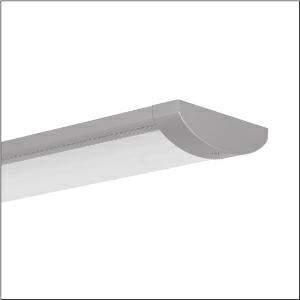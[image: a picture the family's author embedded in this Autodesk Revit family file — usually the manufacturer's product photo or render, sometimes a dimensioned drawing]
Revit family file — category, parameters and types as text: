
# Revit family: tv_20_5xa861d4n0x
name_source: partatom
category: Lighting Fixtures
units: mm (PartAtom-declared; Revit-internal decimal feet)

## family parameters
Cut with Voids When Loaded = No
Host = Face
Light Source = No
Part Type = Normal
Room Calculation Point = No
Round Connector Dimension = Use Diameter
Shared = No

## types (1)
- TV 20 (1 x LED 4000K / CRI = 80 (unbekannt), 5120 lm, 4000K)
    Apparent Load = 50 VA
    CIE Flux Codes = 48 78 95 99 100
    Color Rendering = 80
    Color Temperature = 4000K
    Default Elevation = 1800 mm
    Description = TV 20, vandal-proof luminaire, primary light control with specular reflector, of aluminium, matt, primary optical cover: enclosure, of PC, frosted, light emission: direct distribution, primary light characteristic: symmetric, installation type: surface-mounted, LED, rated luminous flux: 5.120lm, luminous efficacy: 102lm/W, light colour: 840, colour temperature: 4000K, control gear: ECG DALI, mains connection: 230V, AC, 50Hz, rated input power: 50W, luminaire housing, of aluminium, coated, Siteco® metallic grey (DB 702S), with wall and ceiling fixing element, length: 1.561mm, width: 260mm, height: 70mm, protection rating (complete): IP65, insulation class (complete): insulation class I (protective earthing), certification: CE, protection symbol: F, impact resistance: 2x IK10, standard: EN 60598, packaging unit: 1 piece
    Height = 70 mm
    Lamp = 1 x LED 4000K / CRI >= 80 (unbekannt)
    Lamp Light Flux = 5120 lm
    Lamp count = 1
    Length = 1561 mm
    Luminous efficacy = 102 lm/W
    Manufacturer = Siteco
    ModVariant = No
    Model = 5XA861D4N0X
    Mounting Place = Ceiling
    Mounting Type = Surface mounted
    Number of Poles = 1
    OnlyDefault = Yes
    Power Factor = 1
    Product Name = TV 20
    Product group = vandal-proof luminaire
    ProductGroupID = 307
    Protection Class = Protection class I
    Protection Degree = IP 65
    RLX_Detail_Level = 1
    RLX_Emergency_Light_Flux = 0 lm
    RLX_Emergency_Type = 0
    RLX_Emergency_Type_DB = No
    RlxData = <blob elided: 25281 chars, md5=1df7c23b>
    Socket = socket
    Standby Power = 0 W
    System Light Flux = 5120 lm
    System Power = 50 W
    Type Comments = Product without accessories
    Type Image = l_1004809.jpg
    URL = http://relux.com
    VarID = ---
    Voltage = 0 V
    Weight = 0.00 kg
    Width = 260 mm

## geometry (parser evidence)
native form markers: Blend x4, Sweep x10
no freeform markers — native parametric forms only
